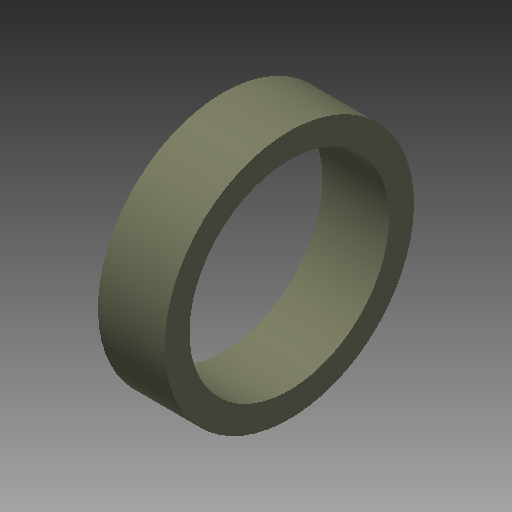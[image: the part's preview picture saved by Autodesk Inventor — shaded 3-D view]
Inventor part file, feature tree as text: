
AUTODESK INVENTOR PART (.ipt)
format: ipt  version: 2019 (Build 230136000, 136)  size: 105,472 bytes
history: native  units: mm
features: other x7, revolve x1, sketch x1
ambient origin geometry x8: Origin, YZ Plane, XZ Plane, XY Plane, X Axis, Y Axis, Z Axis, Center Point
bodies: Solid1 (feature_tree)
feature tree (9):
  revolve  "Revolution1"  [1 undecoded]
  other  "k_c_XY"
  other  "k_c_YZ"
  other  "k_c_ZX"
  other  "k_c_X"
  other  "k_c_Y"
  other  "k_c_Z"
  other  "k_c_Center"
  sketch  "Sketch_1"  dims[d0=360.0deg]
note: 1 required parameter value undecoded (feature->parameter linkage not recoverable at this tier; creation-order binding heuristic only, values carry confidence <= 0.55)
